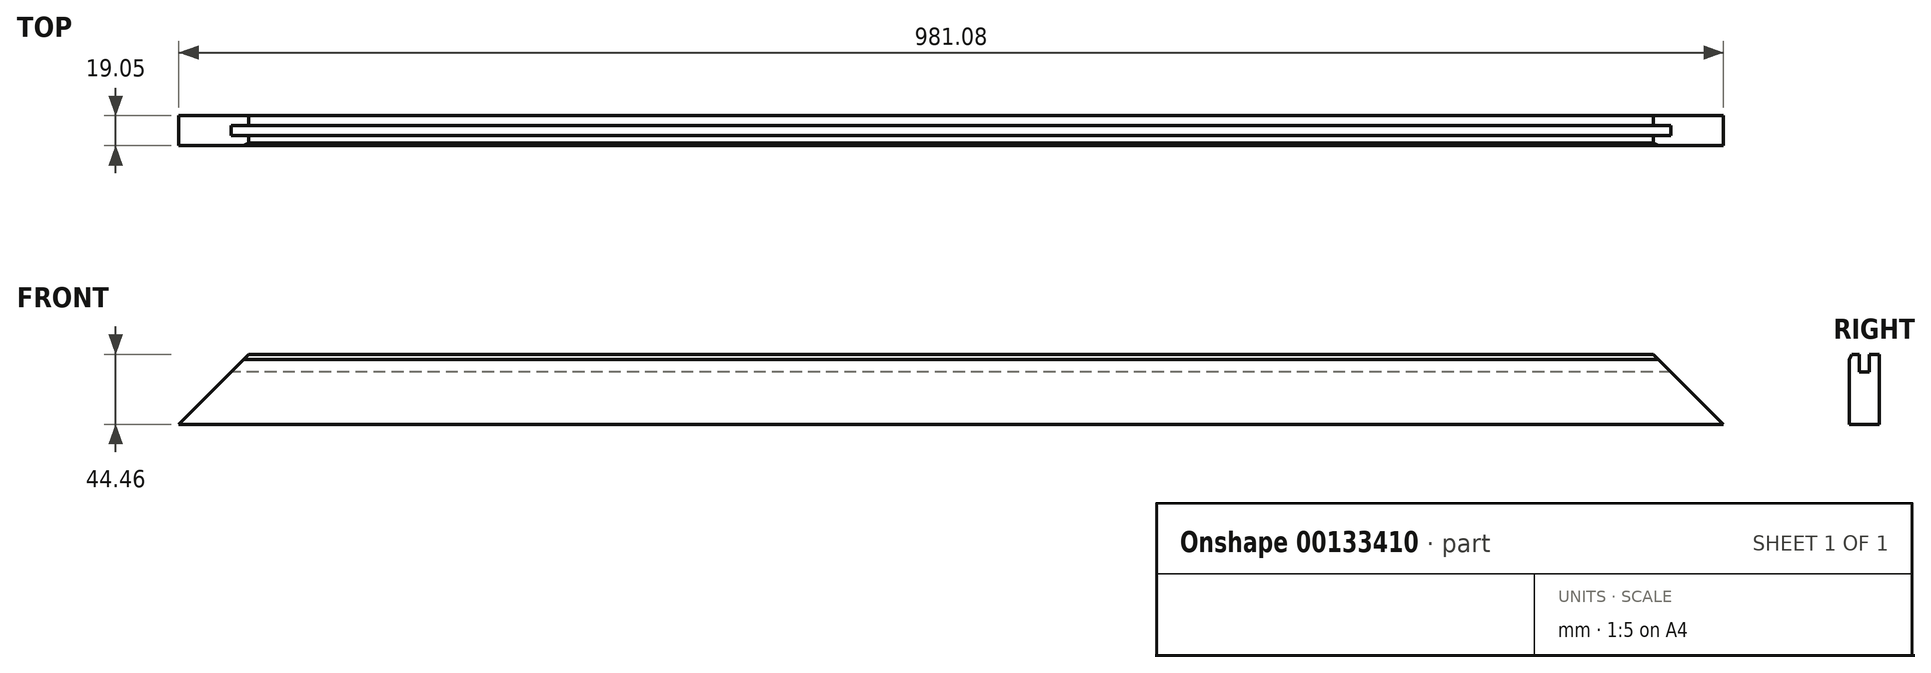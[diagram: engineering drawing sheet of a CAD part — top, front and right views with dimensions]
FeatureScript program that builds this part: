
annotation { "Feature Type Name" : "Feature", "Feature Type Description" : "" }
export const myFeature = defineFeature(function(context is Context, id is Id, definition is map)
    precondition{}
    {
        {
            var Q0;
            Q0=qCreatedBy(makeId("Front.planeOp"),FACE);
            var sketch = newSketch(context, id + "F0", { "sketchPlane" : qUnion([Q0])});
            skLineSegment(sketch, "E0.bottom", {"start": v(-490.54, 22.23) * mm, "end": v(490.54, 22.23) * mm});
            skLineSegment(sketch, "E0.top", {"start": v(-490.54, -22.23) * mm, "end": v(490.54, -22.23) * mm});
            skLineSegment(sketch, "E0.left", {"start": v(-490.54, 22.23) * mm, "end": v(-490.54, -22.23) * mm});
            skLineSegment(sketch, "E0.right", {"start": v(490.54, 22.23) * mm, "end": v(490.54, -22.23) * mm});
            skPoint(sketch, "E0.middle", {"position": v(0, 0) * mm});
            skLineSegment(sketch, "E1", {"start": v(-490.54, -22.23) * mm, "end": v(-446.09, 22.23) * mm, "construction": true});
            skLineSegment(sketch, "E2", {"start": v(490.54, -22.23) * mm, "end": v(446.09, 22.23) * mm, "construction": true});
            skLineSegment(sketch, "E3", {"start": v(-457.2, 11.11) * mm, "end": v(-490.54, 11.11) * mm, "construction": true});
            skLineSegment(sketch, "E4", {"start": v(457.2, 11.11) * mm, "end": v(490.54, 11.11) * mm, "construction": true});
            skSolve(sketch);
        }
        {
            var Q0;
            Q0=qSketchRegion(id+"F0",true);
            extrude(context, id + "F1", {"entities" : qUnion([Q0]), "depth" : 19.05 * mm});
        }
        {
            var Q0;
            Q0=makeQuery(id+"F1.opExtrude","SWEPT_FACE",FACE,{"disambiguationData":[OSD([sQuery(id+"F0.wireOp",EDGE,"E0.left")])]});
            var sketch = newSketch(context, id + "F2", { "sketchPlane" : qUnion([Q0])});
            skLineSegment(sketch, "E5", {"start": v(9.53, 22.23) * mm, "end": v(9.53, -22.22) * mm, "construction": true});
            skLineSegment(sketch, "E6.bottom", {"start": v(6.35, 22.23) * mm, "end": v(12.7, 22.23) * mm});
            skLineSegment(sketch, "E6.top", {"start": v(6.35, 11.11) * mm, "end": v(12.7, 11.11) * mm});
            skLineSegment(sketch, "E6.left", {"start": v(6.35, 22.23) * mm, "end": v(6.35, 11.11) * mm});
            skLineSegment(sketch, "E6.right", {"start": v(12.7, 22.23) * mm, "end": v(12.7, 11.11) * mm});
            skSolve(sketch);
        }
        {
            var Q0;
            Q0=qSketchRegion(id+"F2",true);
            extrude(context, id + "F3", {"entities" : qUnion([Q0]), "operationType" : NewBodyOperationType.REMOVE, "endBound" : BoundingType.THROUGH_ALL, "oppositeDirection" : true, "depth" : 25.4 * mm});
        }
        {
            var Q0;
            Q0=makeQuery(id+"F1.opExtrude","CAP_EDGE",EDGE,{"disambiguationData":[OSD([sQuery(id+"F0.wireOp",EDGE,"E0.bottom")])],"isStart":false});
            chamfer(context, id + "F4", {"entities" : qUnion([Q0]), "chamferType" : ChamferType.TWO_OFFSETS, "width1" : 1.59 * mm, "oppositeDirection" : false, "width2" : 3.17 * mm, "tangentPropagation" : true});
        }
        {
            var Q0;
            Q0=makeQuery(id+"F1.opExtrude","CAP_FACE",FACE,{"disambiguationData":[OSD([sQuery(id+"F0.wireOp",EDGE,"E0.bottom"),sQuery(id+"F0.wireOp",EDGE,"E0.top"),sQuery(id+"F0.wireOp",EDGE,"E0.left"),sQuery(id+"F0.wireOp",EDGE,"E0.right")])],"isStart":true});
            var sketch = newSketch(context, id + "F5", { "sketchPlane" : qUnion([Q0])});
            skLineSegment(sketch, "E7", {"start": v(-490.54, -22.23) * mm, "end": v(-446.09, 22.23) * mm});
            skLineSegment(sketch, "E8", {"start": v(-446.09, 22.23) * mm, "end": v(-490.54, 22.23) * mm});
            skLineSegment(sketch, "E9", {"start": v(-490.54, 22.23) * mm, "end": v(-490.54, -22.23) * mm});
            skLineSegment(sketch, "E10", {"start": v(0, 22.23) * mm, "end": v(0, -22.23) * mm, "construction": true});
            skLineSegment(sketch, "E11.MirrorCS", {"start": v(490.54, -22.22) * mm, "end": v(446.09, 22.23) * mm});
            skLineSegment(sketch, "E12.MirrorCS", {"start": v(490.54, 22.23) * mm, "end": v(490.54, -22.23) * mm});
            skLineSegment(sketch, "E13.MirrorCS", {"start": v(446.09, 22.23) * mm, "end": v(490.54, 22.23) * mm});
            skSolve(sketch);
        }
        {
            var Q0;
            Q0=qSketchRegion(id+"F5",true);
            extrude(context, id + "F6", {"entities" : qUnion([Q0]), "operationType" : NewBodyOperationType.REMOVE, "endBound" : BoundingType.THROUGH_ALL, "oppositeDirection" : true, "depth" : 25.4 * mm});
        }
    });
